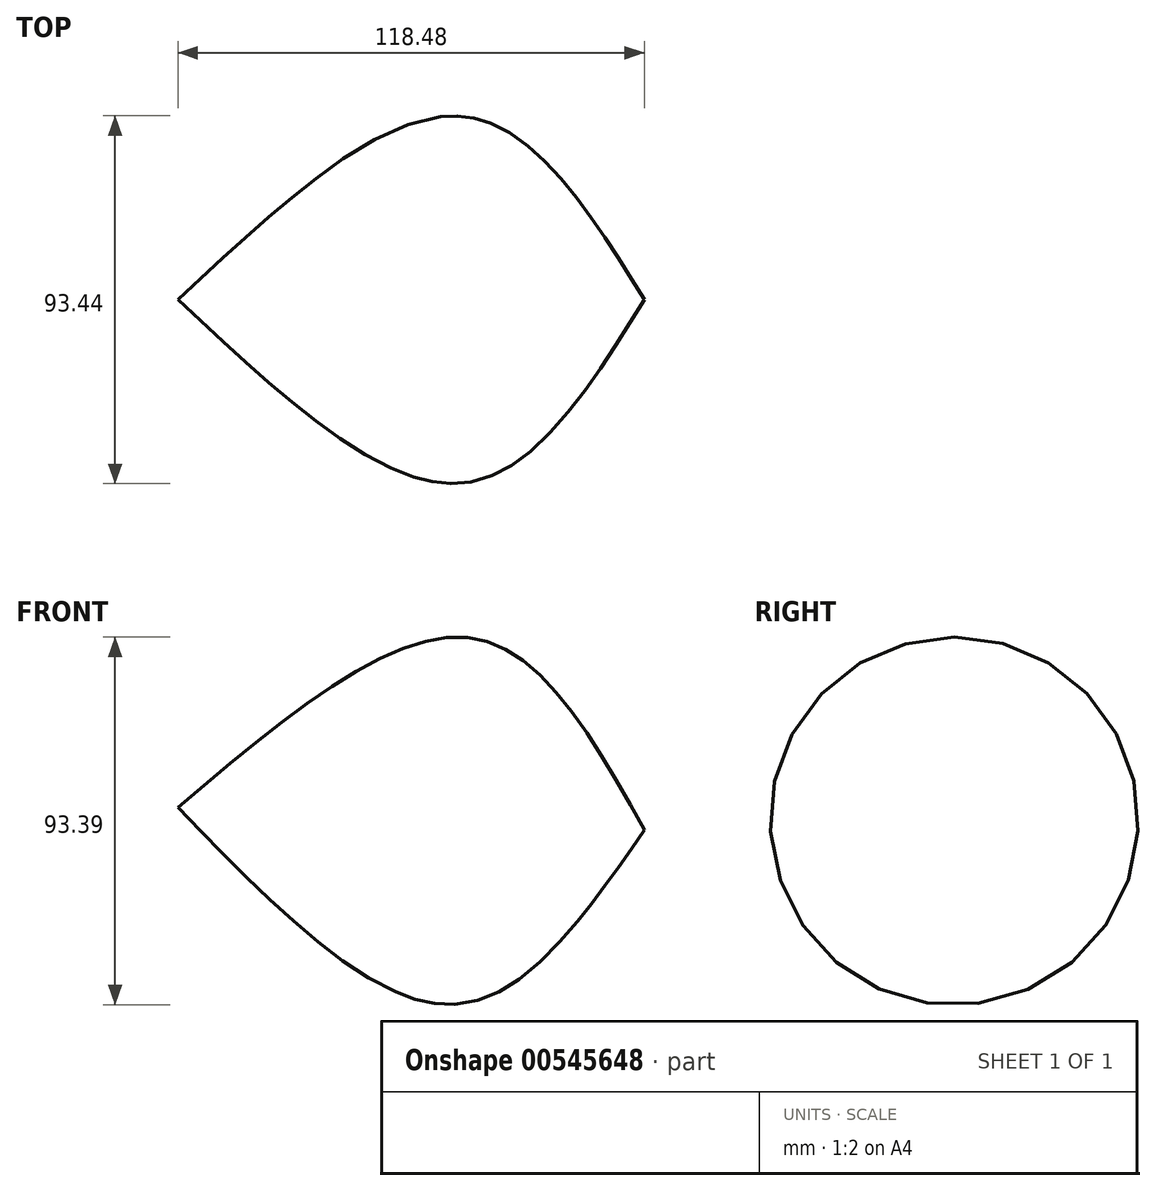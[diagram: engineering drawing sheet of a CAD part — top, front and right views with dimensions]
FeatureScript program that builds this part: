
annotation { "Feature Type Name" : "Feature", "Feature Type Description" : "" }
export const myFeature = defineFeature(function(context is Context, id is Id, definition is map)
    precondition{}
    {
        {
            var Q0;
            Q0=qCreatedBy(makeId("Front.planeOp"),FACE);
            var sketch = newSketch(context, id + "F0", { "sketchPlane" : qUnion([Q0])});
            skFitSpline(sketch, "E0", {"points": [v(-60.12, 13.16) * mm, v(14.92, 56.17) * mm, v(58.36, 7.46) * mm], "startDerivative": vector(152.73, 129.9) * mm, "endDerivative": vector(82.58, -147.8) * mm});
            skLineSegment(sketch, "E1", {"start": v(-60.12, 13.16) * mm, "end": v(58.36, 7.46) * mm});
            skSolve(sketch);
        }
        {
            var Q0;
            Q0 = qSketchRegion(id + "F0", true);
            var Q1;
            Q1=sQuery(id+"F0.wireOp",EDGE,"E1");
            revolve(context, id + "F1", {"entities" : qUnion([Q0]), "axis" : qUnion([Q1]), "revolveType" : RevolveType.FULL});
        }
    });
